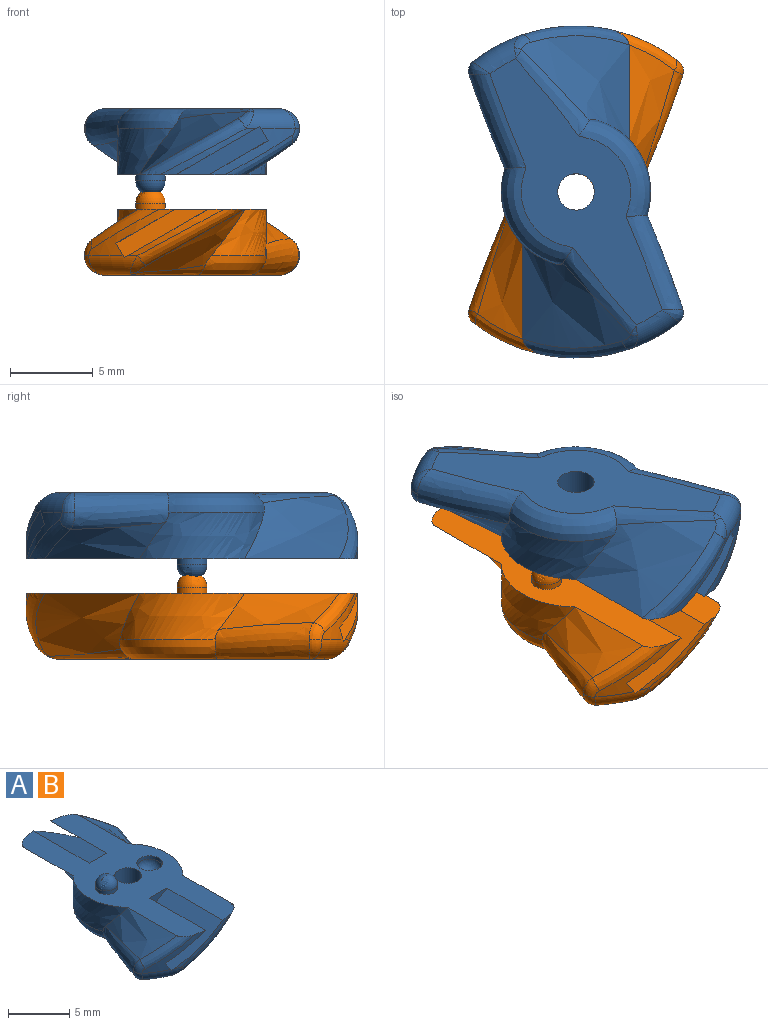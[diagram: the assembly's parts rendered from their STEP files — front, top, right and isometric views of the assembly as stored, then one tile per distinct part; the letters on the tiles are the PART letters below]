
ASSEMBLY  parts=2 mates=1
PART A: 46 faces, bbox 19.9x20.9x7.5 mm
  f0: cylinder r=10mm len=5.8mm, axis (0,0,-1), area 2.2mm2, adj f6,f13,f28,f34
  f1: cylinder r=10mm len=5.22mm, axis (0,0,-1), area 3.5mm2, adj f6,f7,f8,f29,f41,f43
  f2: plane 16.04x10.38mm, normal (0,0,-1), area 62.1mm2, adj f5,f31,f33,f34,f36,f40,f41,f42
  f3: cylinder r=10mm len=5.8mm, axis (0,0,-1), area 2.2mm2, adj f6,f9,f27,f41
  f4: cylinder r=10mm len=5.22mm, axis (0,0,-1), area 3.5mm2, adj f6,f11,f12,f26,f30,f34
  f5: cylinder r=1.1mm len=4mm, axis (0,0,-1), area 27.6mm2, adj f2,f6
  f6: plane 20.15x9.25mm, normal (0,0,1), area 100.7mm2, adj f0,f1,f3,f4,f5,f8,f9,f10
  f7: plane 5.63x0.87mm, normal (-0.87,0,0.5), area 5.5mm2, adj f1,f8,f9,f10,f41
  f8: plane 6.51x3.64mm, normal (-0.5,0,-0.87), area 25mm2, adj f1,f6,f7,f10
  f9: plane 6.56x5.14mm, normal (0.5,0,0.87), area 36.8mm2, adj f3,f6,f7,f10,f41
  f10: plane 5.58x2.93mm, normal (0,1,0), area 5mm2, adj f6,f7,f8,f9
  f11: plane 5.63x0.87mm, normal (0.87,0,0.5), area 5.5mm2, adj f4,f12,f13,f14,f34
  f12: plane 6.51x3.64mm, normal (0.5,0,-0.87), area 25mm2, adj f4,f6,f11,f14
  f13: plane 6.56x5.14mm, normal (-0.5,0,0.87), area 36.8mm2, adj f0,f6,f11,f14,f34
  f14: plane 5.58x2.93mm, normal (0,-1,0), area 5mm2, adj f6,f11,f12,f13
  f15: cylinder r=1.05mm len=2.1mm, axis (0,0,1), area 2.3mm2, adj f6,f19
  f16: plane 0.3x0.3mm, normal (0,0,1), area 0.1mm2, adj f19
  f17: cylinder r=0.9mm len=1.8mm, axis (0,0,-1), area 2mm2, adj f6,f18
  f18: sphere r=0.9mm, area 5.1mm2, adj f17
  f19: torus R=0.15mm, axis (0,0,1), area 6.4mm2, adj f15,f16
  f20: bspline ~8.38x6.53mm, area 19.7mm2, adj f6,f21,f22,f42,f45
  f21: bspline ~8.33x4.31mm, area 17mm2, adj f6,f20,f29,f45
  f22: bspline ~9.81x7.41mm, area 31.6mm2, adj f6,f20,f28,f35,f40,f42
  f23: bspline ~8.38x6.53mm, area 19.7mm2, adj f6,f24,f25,f31,f33
  f24: bspline ~8.33x4.31mm, area 17mm2, adj f6,f23,f26,f31
  f25: bspline ~9.81x7.41mm, area 31.6mm2, adj f6,f23,f27,f33,f36,f38
  f26: bspline ~5.3x3.59mm, area 4.3mm2, adj f4,f6,f24,f30
  f27: bspline ~8.85x5.27mm, area 6.4mm2, adj f3,f6,f25,f38
  f28: bspline ~8.85x5.27mm, area 6.4mm2, adj f0,f6,f22,f35
  f29: bspline ~5.3x3.59mm, area 4.3mm2, adj f1,f6,f21,f43
  f30: bspline ~1.39x1.02mm, area 0.9mm2, adj f4,f26,f31,f32
  f31: bspline ~7.83x6.96mm, area 17.3mm2, adj f2,f23,f24,f30,f32,f33
  f32: bspline ~1.5x1.42mm, area 1.1mm2, adj f30,f31,f34
  f33: bspline ~7.32x4.67mm, area 13.7mm2, adj f2,f23,f25,f31,f36
  f34: torus R=8.8mm, axis (0,0,1), area 4.9mm2, adj f0,f2,f4,f11,f13,f32,f35,f37
  f35: bspline ~1.5x1.27mm, area 0.8mm2, adj f22,f28,f34,f37
  f36: bspline ~6.77x6.1mm, area 5.6mm2, adj f2,f25,f33,f39
  f37: bspline ~0.91x0.57mm, area 0.2mm2, adj f34,f35,f40
  f38: bspline ~1.5x1.27mm, area 0.8mm2, adj f25,f27,f39,f41
  f39: bspline ~0.91x0.57mm, area 0.2mm2, adj f36,f38,f41
  f40: bspline ~6.77x6.1mm, area 5.6mm2, adj f2,f22,f37,f42
  f41: torus R=8.8mm, axis (0,0,1), area 4.9mm2, adj f1,f2,f3,f7,f9,f38,f39,f44
  f42: bspline ~7.32x4.67mm, area 13.7mm2, adj f2,f20,f22,f40,f45
  f43: bspline ~1.39x1.02mm, area 0.9mm2, adj f1,f29,f44,f45
  f44: bspline ~1.5x1.42mm, area 1.1mm2, adj f41,f43,f45
  f45: bspline ~7.83x6.96mm, area 17.3mm2, adj f2,f20,f21,f42,f43,f44
PART B: same geometry as A
PLACE A rot(axis=(1,0,0),180deg) t=(0,0,21.63)mm
PLACE B t=(0,0,11.58)mm
MATE parallel B.f10 <-> A.f14  axis (0,1,0) through (0,3.5,15.58)mm
